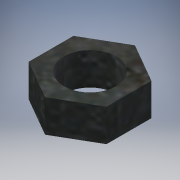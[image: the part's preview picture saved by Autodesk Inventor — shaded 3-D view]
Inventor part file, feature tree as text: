
AUTODESK INVENTOR PART (.ipt)
format: ipt  version: 2016 (Build 200138000, 138)  size: 112,128 bytes
history: native  units: in
note: dims shown in document units (in); Inventor stores cm internally (conversion verified against a paired STEP export)
features: extrude x1, sketch x1
ambient origin geometry x8: Origin, YZ Plane, XZ Plane, XY Plane, X Axis, Y Axis, Z Axis, Center Point
bodies: Solid1 (feature_tree)
feature tree (2):
  extrude  "Extrusion1"  Depth=0.2344in
  sketch  "Sketch1"  dims[d0=0.5625in d1=0.375in d2=0.2344in d3=0.0in]
